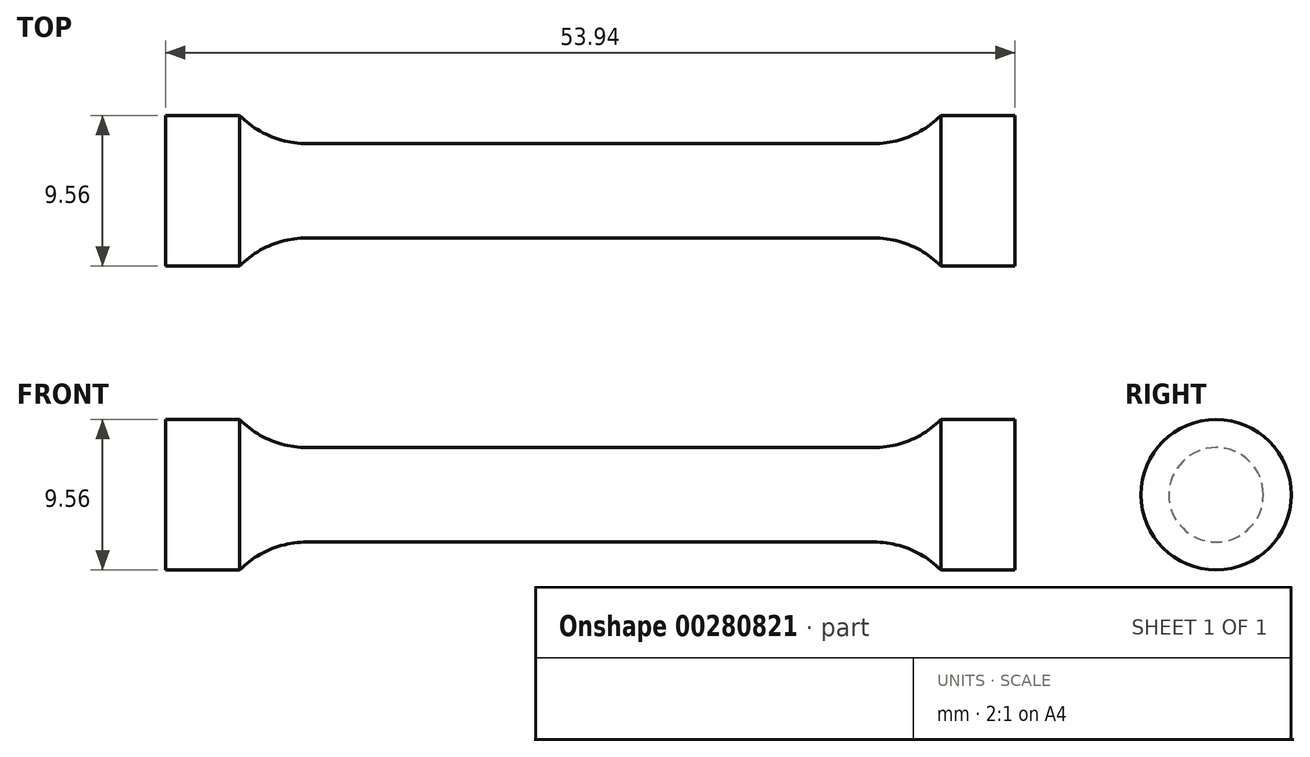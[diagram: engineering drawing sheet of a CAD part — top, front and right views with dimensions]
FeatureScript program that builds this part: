
annotation { "Feature Type Name" : "Feature", "Feature Type Description" : "" }
export const myFeature = defineFeature(function(context is Context, id is Id, definition is map)
    precondition{}
    {
        {
            var Q0;
            Q0=qCreatedBy(makeId("Front.planeOp"),FACE);
            var sketch = newSketch(context, id + "F0", { "sketchPlane" : qUnion([Q0])});
            skLineSegment(sketch, "E0", {"start": v(0, 0) * mm, "end": v(0, 3) * mm});
            skLineSegment(sketch, "E1", {"start": v(0, 3) * mm, "end": v(18, 3) * mm});
            skArc(sketch, "E2", {"start": v(18, 3) * mm, "mid": v(20.3, 3.46) * mm, "end": v(22.26, 4.78) * mm});
            skLineSegment(sketch, "E3", {"start": v(22.26, 4.78) * mm, "end": v(26.97, 4.78) * mm});
            skLineSegment(sketch, "E4", {"start": v(26.97, 4.78) * mm, "end": v(26.97, 0) * mm});
            skArc(sketch, "E5.MirrorCS", {"start": v(-18, 3) * mm, "mid": v(-20.3, 3.46) * mm, "end": v(-22.26, 4.78) * mm});
            skLineSegment(sketch, "E6.MirrorCS", {"start": v(-22.26, 4.78) * mm, "end": v(-26.97, 4.78) * mm});
            skLineSegment(sketch, "E7.MirrorCS", {"start": v(0, 3) * mm, "end": v(-18, 3) * mm});
            skLineSegment(sketch, "E8.MirrorCS", {"start": v(-26.97, 4.78) * mm, "end": v(-26.97, 0) * mm});
            skLineSegment(sketch, "E9", {"start": v(-26.97, 0) * mm, "end": v(26.97, 0) * mm});
            skSolve(sketch);
        }
        {
            var Q0;
            Q0 = qSketchRegion(id + "F0", true);
            var Q1;
            Q1=sQuery(id+"F0.wireOp",EDGE,"E9");
            revolve(context, id + "F1", {"entities" : qUnion([Q0]), "axis" : qUnion([Q1]), "revolveType" : RevolveType.FULL});
        }
    });
